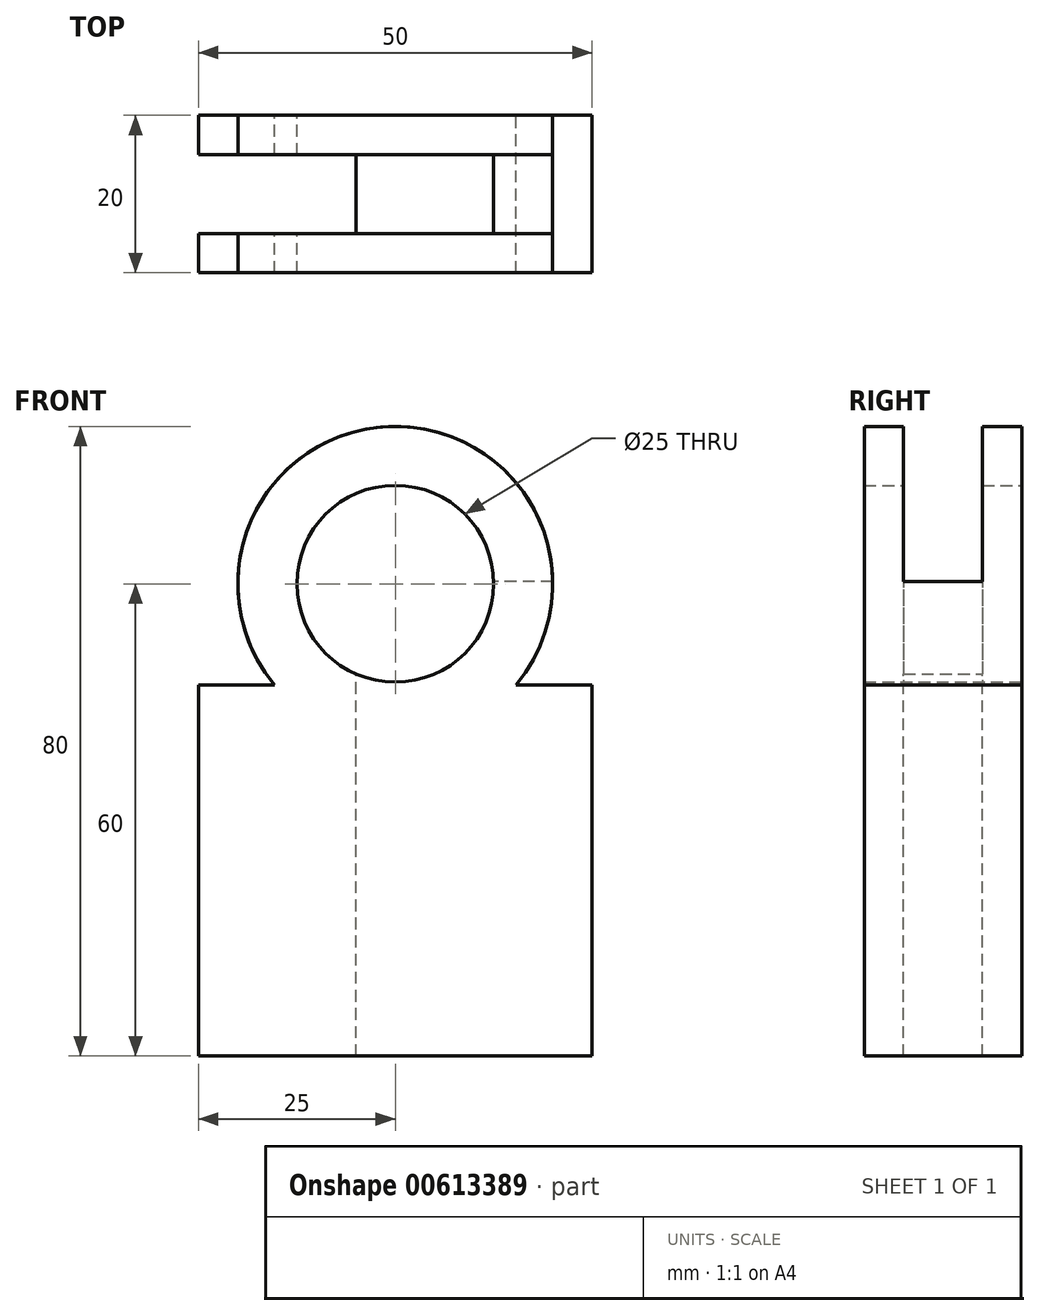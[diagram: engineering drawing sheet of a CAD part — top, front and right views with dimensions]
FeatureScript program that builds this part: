
annotation { "Feature Type Name" : "Feature", "Feature Type Description" : "" }
export const myFeature = defineFeature(function(context is Context, id is Id, definition is map)
    precondition{}
    {
        {
            var Q0;
            Q0=qCreatedBy(makeId("Front.planeOp"),FACE);
            var sketch = newSketch(context, id + "F0", { "sketchPlane" : qUnion([Q0])});
            skLineSegment(sketch, "E0.bottom", {"start": v(0, 0) * mm, "end": v(50, 0) * mm});
            skLineSegment(sketch, "E0.top", {"start": v(0, 47.16) * mm, "end": v(9.67, 47.16) * mm});
            skLineSegment(sketch, "E0.left", {"start": v(0, 0) * mm, "end": v(0, 47.16) * mm});
            skLineSegment(sketch, "E0.right", {"start": v(50, 0) * mm, "end": v(50, 47.16) * mm});
            skArc(sketch, "E1", {"start": v(40.33, 47.16) * mm, "mid": v(25, 80) * mm, "end": v(9.67, 47.16) * mm});
            skPoint(sketch, "E1.centerSnap0", {"position": v(25, 47.16) * mm});
            skLineSegment(sketch, "E2.trimOffspring", {"start": v(40.33, 47.16) * mm, "end": v(50, 47.16) * mm});
            skCircle(sketch, "E3", {"center": v(25, 60) * mm, "radius": 12.5 * mm});
            skSolve(sketch);
        }
        {
            var Q0;
            Q0 = qSketchRegion(id + "F0", true);
            extrude(context, id + "F1", {"entities" : qUnion([Q0]), "endBound" : BoundingType.SYMMETRIC, "depth" : 20 * mm, "offsetDistance" : 25 * mm});
        }
        {
            var Q0;
            Q0=makeQuery(id+"F1.opExtrude","SWEPT_FACE",FACE,{"disambiguationData":[OSD([sQuery(id+"F0.wireOp",EDGE,"E0.left")])]});
            var sketch = newSketch(context, id + "F2", { "sketchPlane" : qUnion([Q0])});
            skLineSegment(sketch, "E4.bottom", {"start": v(-5, 0) * mm, "end": v(5, 0) * mm});
            skLineSegment(sketch, "E4.top", {"start": v(-5, 90.44) * mm, "end": v(5, 90.44) * mm});
            skLineSegment(sketch, "E4.left", {"start": v(-5, 0) * mm, "end": v(-5, 90.44) * mm});
            skLineSegment(sketch, "E4.right", {"start": v(5, 0) * mm, "end": v(5, 90.44) * mm});
            skSolve(sketch);
        }
        {
            var Q0;
            Q0 = qSketchRegion(id + "F2", true);
            extrude(context, id + "F3", {"entities" : qUnion([Q0]), "operationType" : NewBodyOperationType.REMOVE, "endBound" : BoundingType.SYMMETRIC, "oppositeDirection" : true, "depth" : 40 * mm, "offsetDistance" : 25 * mm});
        }
        {
            var Q0;
            {var subQ0=sQuery(id+"F2.wireOp",EDGE,"E4.right");var subQ1=sQuery(id+"F2.wireOp",EDGE,"E4.left");Q0=makeQuery(id+"F3.boolean.opBoolean","COPY",FACE,{"disambiguationData":[TD([makeQuery(id+"F1.opExtrude","SWEPT_FACE",FACE,{"disambiguationData":[OSD([sQuery(id+"F0.wireOp",EDGE,"E1")])]})])],"derivedFrom":makeQuery(id+"F3.opExtrude","CAP_FACE",FACE,{"disambiguationData":[OSD([sQuery(id+"F2.wireOp",EDGE,"E4.bottom"),sQuery(id+"F2.wireOp",EDGE,"E4.top"),subQ1,subQ0])],"isStart":false})});}
            var sketch = newSketch(context, id + "F4", { "sketchPlane" : qUnion([Q0])});
            skLineSegment(sketch, "E5.bottom", {"start": v(-5, 81.46) * mm, "end": v(5, 84.64) * mm});
            skLineSegment(sketch, "E5.left", {"start": v(-5, 81.46) * mm, "end": v(-5, 71.5) * mm});
            skLineSegment(sketch, "E5.right", {"start": v(5, 84.64) * mm, "end": v(5, 71.46) * mm});
            skLineSegment(sketch, "E6", {"start": v(-5, 71.5) * mm, "end": v(-5, 60.32) * mm});
            skLineSegment(sketch, "E7", {"start": v(5, 71.46) * mm, "end": v(5, 60.32) * mm});
            skLineSegment(sketch, "E8", {"start": v(5, 60.32) * mm, "end": v(-5, 60.32) * mm});
            skSolve(sketch);
        }
        {
            var Q0;
            Q0 = qSketchRegion(id + "F4", true);
            extrude(context, id + "F5", {"entities" : qUnion([Q0]), "operationType" : NewBodyOperationType.REMOVE, "endBound" : BoundingType.THROUGH_ALL, "oppositeDirection" : true, "depth" : 25 * mm, "offsetDistance" : 25 * mm});
        }
    });
